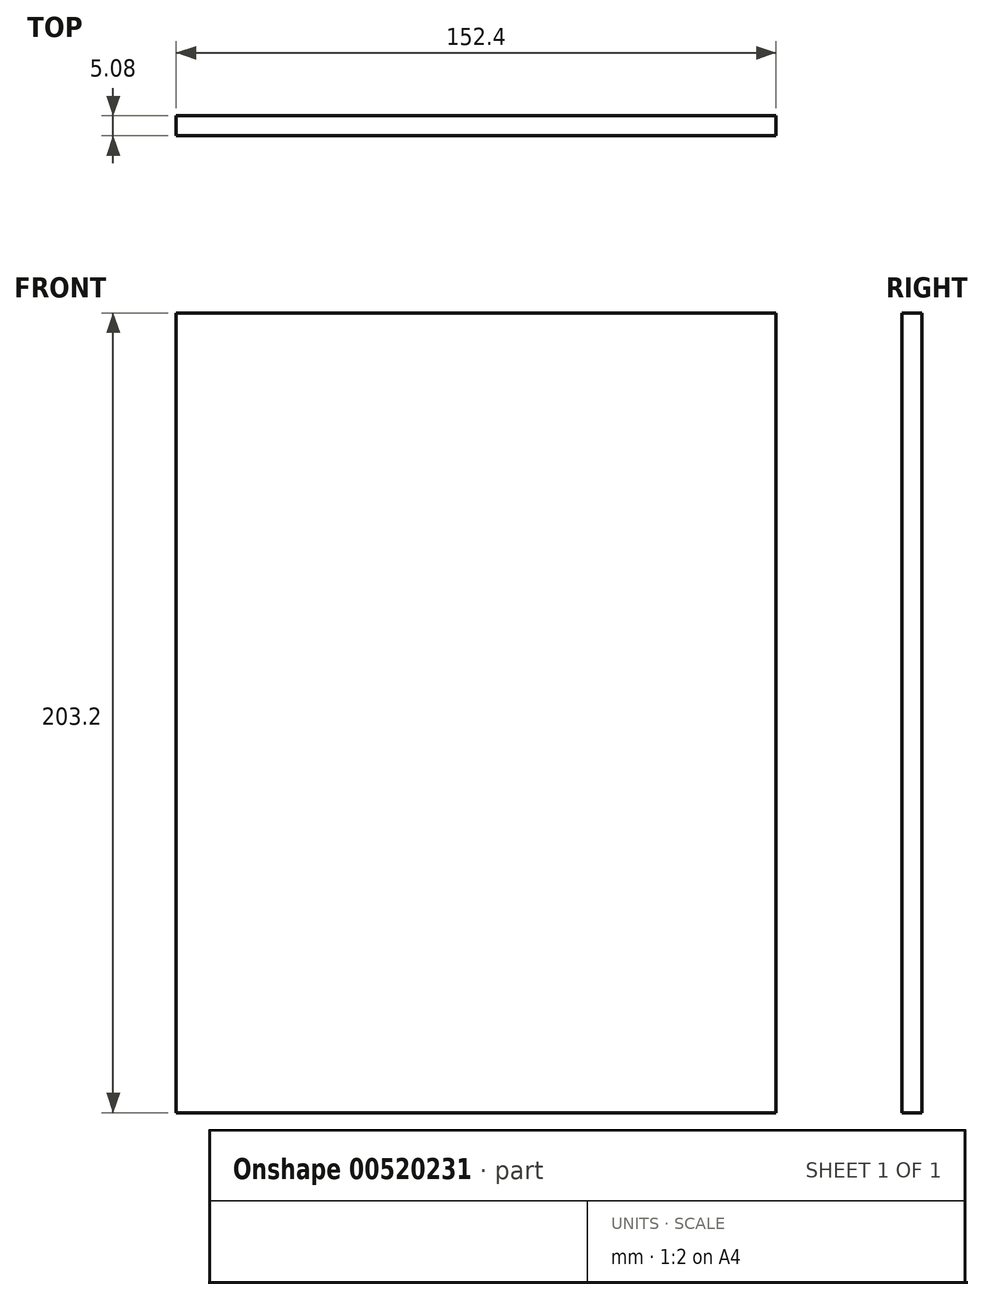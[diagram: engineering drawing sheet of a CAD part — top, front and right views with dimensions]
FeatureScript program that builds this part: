
annotation { "Feature Type Name" : "Feature", "Feature Type Description" : "" }
export const myFeature = defineFeature(function(context is Context, id is Id, definition is map)
    precondition{}
    {
        {
            var Q0;
            Q0=qCreatedBy(makeId("Front.planeOp"),FACE);
            var sketch = newSketch(context, id + "F0", { "sketchPlane" : qUnion([Q0])});
            skLineSegment(sketch, "E0.bottom", {"start": v(-63.38, 123.5) * mm, "end": v(89.02, 123.5) * mm});
            skLineSegment(sketch, "E0.top", {"start": v(-63.38, -79.7) * mm, "end": v(89.02, -79.7) * mm});
            skLineSegment(sketch, "E0.left", {"start": v(-63.38, 123.5) * mm, "end": v(-63.38, -79.7) * mm});
            skLineSegment(sketch, "E0.right", {"start": v(89.02, 123.5) * mm, "end": v(89.02, -79.7) * mm});
            skSolve(sketch);
        }
        {
            var Q0;
            Q0=makeQuery(id+"F0.imprint","IMPRINT",FACE,{"disambiguationData":[TD([[makeQuery(id+"F0.imprint","IMPRINT",EDGE,{"derivedFrom":sQuery(id+"F0.wireOp",EDGE,"E0.bottom")}),-1.0]])]});
            extrude(context, id + "F1", {"entities" : qUnion([Q0]), "depth" : 5.08 * mm, "offsetDistance" : 25.4 * mm});
        }
    });
